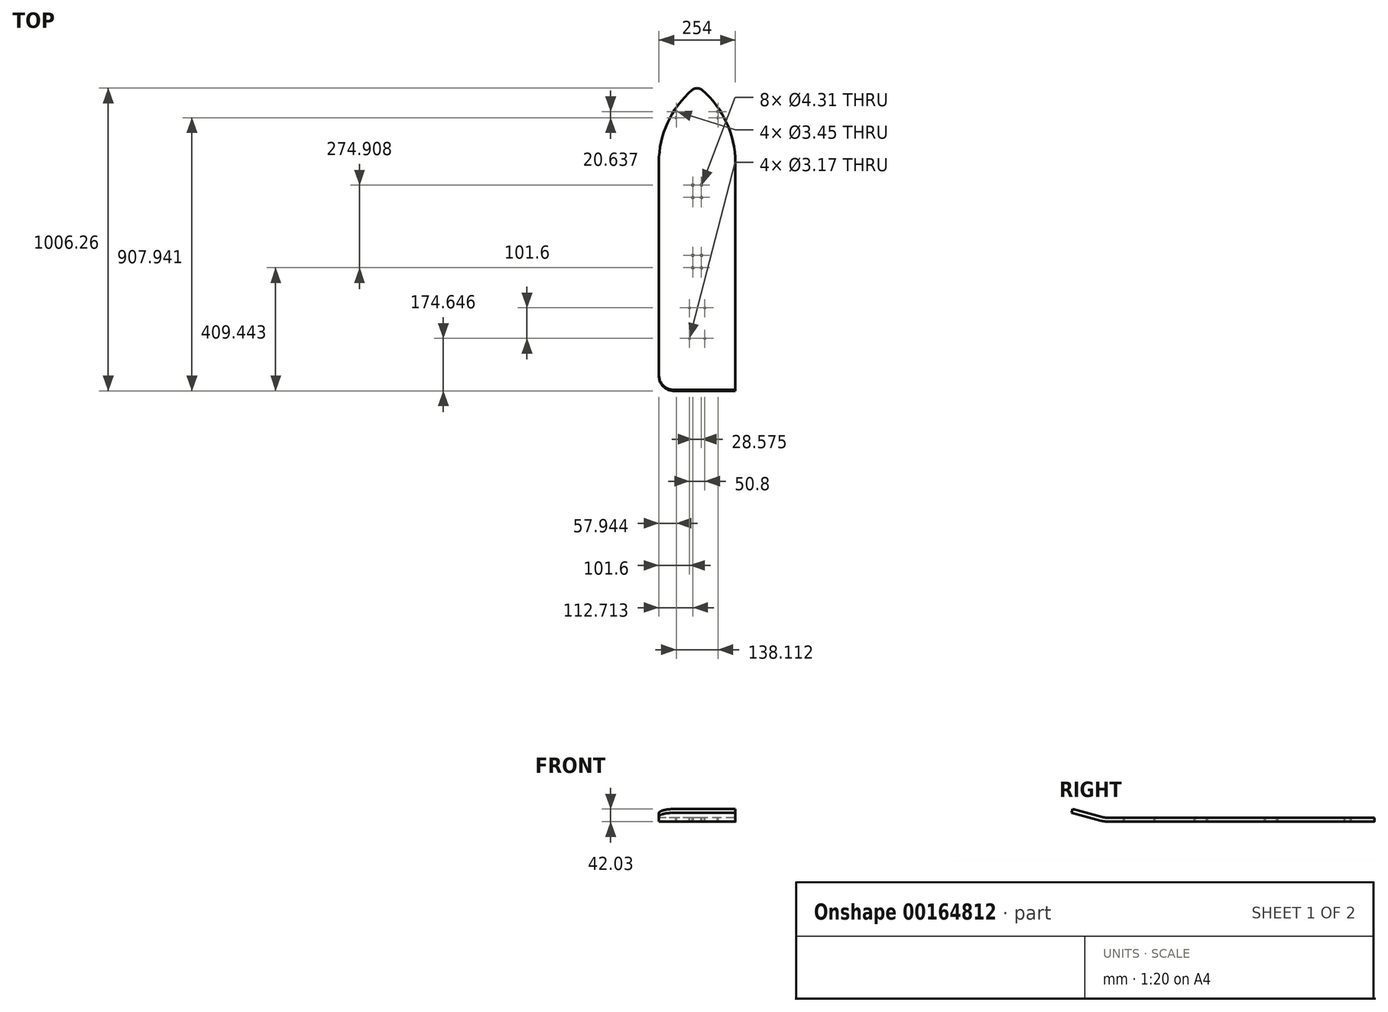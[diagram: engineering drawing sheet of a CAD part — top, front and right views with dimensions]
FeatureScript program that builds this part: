
annotation { "Feature Type Name" : "Feature", "Feature Type Description" : "" }
export const myFeature = defineFeature(function(context is Context, id is Id, definition is map)
    precondition{}
    {
        {
            var Q0;
            Q0=qCreatedBy(makeId("Top.planeOp"),FACE);
            var sketch = newSketch(context, id + "F0", { "sketchPlane" : qUnion([Q0])});
            skLineSegment(sketch, "E0.bottom", {"start": v(0, 0) * mm, "end": v(-254, 0) * mm, "construction": true});
            skLineSegment(sketch, "E0.top", {"start": v(0, -635) * mm, "end": v(-254, -635) * mm});
            skLineSegment(sketch, "E0.left", {"start": v(0, 0) * mm, "end": v(0, -635) * mm});
            skLineSegment(sketch, "E0.right", {"start": v(-254, 0) * mm, "end": v(-254, -635) * mm});
            skArc(sketch, "E1", {"start": v(0, 0) * mm, "mid": v(-33.52, 142) * mm, "end": v(-127, 254) * mm});
            skArc(sketch, "E2", {"start": v(-127, 254) * mm, "mid": v(-220.48, 142) * mm, "end": v(-254, 0) * mm});
            skLineSegment(sketch, "E3", {"start": v(-127, 0) * mm, "end": v(-127, 254) * mm, "construction": true});
            skSolve(sketch);
        }
        {
            var Q0;
            Q0=qSketchRegion(id+"F0",true);
            extrude(context, id + "F1", {"entities" : qUnion([Q0]), "depth" : 12.7 * mm});
        }
        {
            var Q0;
            Q0=makeQuery(id+"F1.opExtrude","SWEPT_EDGE",EDGE,{"disambiguationData":[OSD([sQuery(id+"F0.wireOp",EDGE,"E1"),sQuery(id+"F0.wireOp",EDGE,"E2")])]});
            fillet(context, id + "F2", {"entities" : qUnion([Q0]), "radius" : 25.4 * mm, "tangentPropagation" : true, "allowEdgeOverflow" : false});
        }
        {
            var Q0;
            Q0=makeQuery(id+"F1.opExtrude","SWEPT_FACE",FACE,{"disambiguationData":[OSD([sQuery(id+"F0.wireOp",EDGE,"E0.right")])]});
            var sketch = newSketch(context, id + "F3", { "sketchPlane" : qUnion([Q0])});
            skArc(sketch, "E4", {"start": v(635, 12.7) * mm, "mid": v(646.6, 13.46) * mm, "end": v(658, 15.73) * mm});
            skArc(sketch, "E5", {"start": v(635, 0) * mm, "mid": v(648.26, 0.87) * mm, "end": v(661.3, 3.46) * mm});
            skLineSegment(sketch, "E6", {"start": v(635, 101.6) * mm, "end": v(658, 15.73) * mm, "construction": true});
            skLineSegment(sketch, "E7", {"start": v(658, 15.73) * mm, "end": v(661.3, 3.46) * mm, "construction": true});
            skLineSegment(sketch, "E8.bottom", {"start": v(658, 15.73) * mm, "end": v(756.15, 42.03) * mm});
            skLineSegment(sketch, "E8.top", {"start": v(661.3, 3.46) * mm, "end": v(759.43, 29.76) * mm});
            skLineSegment(sketch, "E8.right", {"start": v(756.15, 42.03) * mm, "end": v(759.43, 29.76) * mm});
            skLineSegment(sketch, "E9", {"start": v(635, 101.6) * mm, "end": v(635, 12.7) * mm, "construction": true});
            skLineSegment(sketch, "E10", {"start": v(635, 12.7) * mm, "end": v(635, 0) * mm});
            skLineSegment(sketch, "E11", {"start": v(635, 0) * mm, "end": v(759.43, 0) * mm, "construction": true});
            skLineSegment(sketch, "E12", {"start": v(759.43, 0) * mm, "end": v(759.43, 29.76) * mm, "construction": true});
            skSolve(sketch);
        }
        {
            var Q0;
            Q0=qSketchRegion(id+"F3",true);
            var Q1;
            Q1=makeQuery(id+"F1.opExtrude","SWEPT_FACE",FACE,{"disambiguationData":[OSD([sQuery(id+"F0.wireOp",EDGE,"E0.left")])]});
            extrude(context, id + "F4", {"entities" : qUnion([Q0]), "operationType" : NewBodyOperationType.ADD, "endBound" : BoundingType.UP_TO_SURFACE, "oppositeDirection" : true, "endBoundEntityFace" : qUnion([Q1]), "depth" : 25.4 * mm});
        }
        {
            var Q0;
            Q0=makeQuery(id+"F4.opExtrude","TWEAK_EDGE",EDGE,{"derivedFrom":[makeQuery(id+"F1.opExtrude","SWEPT_FACE",FACE,{"disambiguationData":[OSD([sQuery(id+"F0.wireOp",EDGE,"E0.left")])]}),makeQuery(id+"F3.imprint","IMPRINT",EDGE,{"derivedFrom":sQuery(id+"F3.wireOp",EDGE,"E8.right")})]});
            var Q1;
            Q1=makeQuery(id+"F4.opExtrude","CAP_EDGE",EDGE,{"disambiguationData":[OSD([sQuery(id+"F3.wireOp",EDGE,"E8.right")])],"isStart":true});
            fillet(context, id + "F5", {"entities" : qUnion([Q0, Q1]), "radius" : 50.8 * mm, "tangentPropagation" : true, "allowEdgeOverflow" : false});
        }
        {
            var Q0;
            Q0=makeQuery(id+"F1.opExtrude","CAP_FACE",FACE,{"disambiguationData":[OSD([sQuery(id+"F0.wireOp",EDGE,"E0.top"),sQuery(id+"F0.wireOp",EDGE,"E0.left"),sQuery(id+"F0.wireOp",EDGE,"E0.right"),sQuery(id+"F0.wireOp",EDGE,"E1"),sQuery(id+"F0.wireOp",EDGE,"E2")])],"isStart":false});
            var sketch = newSketch(context, id + "F6", { "sketchPlane" : qUnion([Q0])});
            skLineSegment(sketch, "E13", {"start": v(-141.29, -308.71) * mm, "end": v(-112.71, -308.71) * mm, "construction": true});
            skLineSegment(sketch, "E14.bottom", {"start": v(-152.4, -483.18) * mm, "end": v(-101.6, -483.18) * mm, "construction": true});
            skLineSegment(sketch, "E14.top", {"start": v(-152.4, -584.78) * mm, "end": v(-101.6, -584.78) * mm, "construction": true});
            skLineSegment(sketch, "E14.left", {"start": v(-152.4, -483.18) * mm, "end": v(-152.4, -584.78) * mm, "construction": true});
            skLineSegment(sketch, "E14.right", {"start": v(-101.6, -483.18) * mm, "end": v(-101.6, -584.78) * mm, "construction": true});
            skLineSegment(sketch, "E15", {"start": v(-127, -584.78) * mm, "end": v(-127, -635) * mm, "construction": true});
            skCircle(sketch, "E16", {"center": v(-112.71, -308.71) * mm, "radius": 2.15 * mm});
            skCircle(sketch, "E17", {"center": v(-141.29, -308.71) * mm, "radius": 2.15 * mm});
            skCircle(sketch, "E18", {"center": v(-101.6, -584.78) * mm, "radius": 1.59 * mm});
            skCircle(sketch, "E19", {"center": v(-152.4, -584.78) * mm, "radius": 1.59 * mm});
            skCircle(sketch, "E20", {"center": v(-152.4, -483.18) * mm, "radius": 1.59 * mm});
            skCircle(sketch, "E21", {"center": v(-101.6, -483.18) * mm, "radius": 1.59 * mm});
            skLineSegment(sketch, "E22", {"start": v(-141.29, -75.08) * mm, "end": v(-112.71, -75.08) * mm, "construction": true});
            skCircle(sketch, "E23", {"center": v(-141.29, -75.08) * mm, "radius": 2.15 * mm});
            skCircle(sketch, "E24", {"center": v(-112.71, -75.08) * mm, "radius": 2.15 * mm});
            skLineSegment(sketch, "E25", {"start": v(-127, -75.08) * mm, "end": v(-127, -116.35) * mm, "construction": true});
            skLineSegment(sketch, "E26", {"start": v(-141.29, -116.35) * mm, "end": v(-112.71, -116.35) * mm, "construction": true});
            skLineSegment(sketch, "E27", {"start": v(-127, -308.71) * mm, "end": v(-127, -349.99) * mm, "construction": true});
            skLineSegment(sketch, "E28", {"start": v(-141.29, -349.99) * mm, "end": v(-112.71, -349.99) * mm, "construction": true});
            skLineSegment(sketch, "E29", {"start": v(-127, -349.99) * mm, "end": v(-127, -483.18) * mm, "construction": true});
            skLineSegment(sketch, "E30", {"start": v(-127, -116.35) * mm, "end": v(-127, -308.71) * mm, "construction": true});
            skCircle(sketch, "E31", {"center": v(-112.71, -116.35) * mm, "radius": 2.15 * mm});
            skCircle(sketch, "E32", {"center": v(-141.29, -116.35) * mm, "radius": 2.15 * mm});
            skCircle(sketch, "E33", {"center": v(-141.29, -349.99) * mm, "radius": 2.15 * mm});
            skCircle(sketch, "E34", {"center": v(-112.71, -349.99) * mm, "radius": 2.15 * mm});
            skLineSegment(sketch, "E35", {"start": v(-127, -75.08) * mm, "end": v(-127, 148.51) * mm, "construction": true});
            skLineSegment(sketch, "E36.bottom", {"start": v(-196.06, 169.15) * mm, "end": v(-57.94, 169.15) * mm, "construction": true});
            skLineSegment(sketch, "E36.top", {"start": v(-196.06, 148.51) * mm, "end": v(-57.94, 148.51) * mm, "construction": true});
            skLineSegment(sketch, "E36.left", {"start": v(-196.06, 169.15) * mm, "end": v(-196.06, 148.51) * mm, "construction": true});
            skLineSegment(sketch, "E36.right", {"start": v(-57.94, 169.15) * mm, "end": v(-57.94, 148.51) * mm, "construction": true});
            skLineSegment(sketch, "E37", {"start": v(-57.94, 169.15) * mm, "end": v(-52.39, 169.15) * mm, "construction": true});
            skLineSegment(sketch, "E38", {"start": v(-52.39, 169.15) * mm, "end": v(-52.39, 174.7) * mm, "construction": true});
            skCircle(sketch, "E39", {"center": v(-57.94, 169.15) * mm, "radius": 1.73 * mm});
            skCircle(sketch, "E40", {"center": v(-57.94, 148.51) * mm, "radius": 1.73 * mm});
            skCircle(sketch, "E41", {"center": v(-196.06, 148.51) * mm, "radius": 1.73 * mm});
            skCircle(sketch, "E42", {"center": v(-196.06, 169.15) * mm, "radius": 1.73 * mm});
            skSolve(sketch);
        }
        {
            var Q0;
            Q0 = qSketchRegion(id + "F6", true);
            var Q1;
            Q1=makeQuery(id+"F1.opExtrude","CAP_FACE",FACE,{"disambiguationData":[OSD([sQuery(id+"F0.wireOp",EDGE,"E0.top"),sQuery(id+"F0.wireOp",EDGE,"E0.left"),sQuery(id+"F0.wireOp",EDGE,"E0.right"),sQuery(id+"F0.wireOp",EDGE,"E1"),sQuery(id+"F0.wireOp",EDGE,"E2")])],"isStart":true});
            extrude(context, id + "F7", {"entities" : qUnion([Q0]), "operationType" : NewBodyOperationType.REMOVE, "endBound" : BoundingType.UP_TO_SURFACE, "oppositeDirection" : true, "endBoundEntityFace" : qUnion([Q1]), "depth" : 25.4 * mm});
        }
    });
